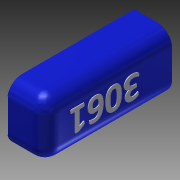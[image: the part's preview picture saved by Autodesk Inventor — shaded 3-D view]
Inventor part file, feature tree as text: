
AUTODESK INVENTOR PART (.ipt)
format: ipt  version: 2013 (Build 170138000, 138)  size: 357,376 bytes
history: native  units: in
note: dims shown in document units (in); Inventor stores cm internally (conversion verified against a paired STEP export)
features: extrude x4, reference x4, sketch x3, fillet x1, projected_geometry x1
ambient origin geometry x8: Origin, YZ Plane, XZ Plane, XY Plane, X Axis, Y Axis, Z Axis, Center Point
bodies: Solid1 (feature_tree)
feature tree (13):
  sketch  "Sketch1"  dims[d0=0.0625in d1=0.0in d3=1.0in]
  extrude  "Extrusion1"  Depth=1.0in
  extrude  "Extrusion2"  Depth=0.0625in
  extrude  "Extrusion3"  Depth=0.0625in TaperAngle=0.0deg
  fillet  "Fillet1"  Radius=1.3125in
  extrude  "Extrusion4"  Depth=6.0in
  reference  "Reference4"
  reference  "Reference5"
  sketch  "Sketch2"  dims[d7=1.0in d9=0.0625in]
  sketch  "Sketch3"  dims[d10=11.25in d11=0.0in d12=0.0625in d13=0.0in d14=1.3125in d15=6.0in d17=1.0in d18=0.0625in d19=0.0in d20=0.0625in d21=0.0625in]
  reference  "Reference6"
  projected_geometry  "Projected Loop1"
  reference  "Reference7"
